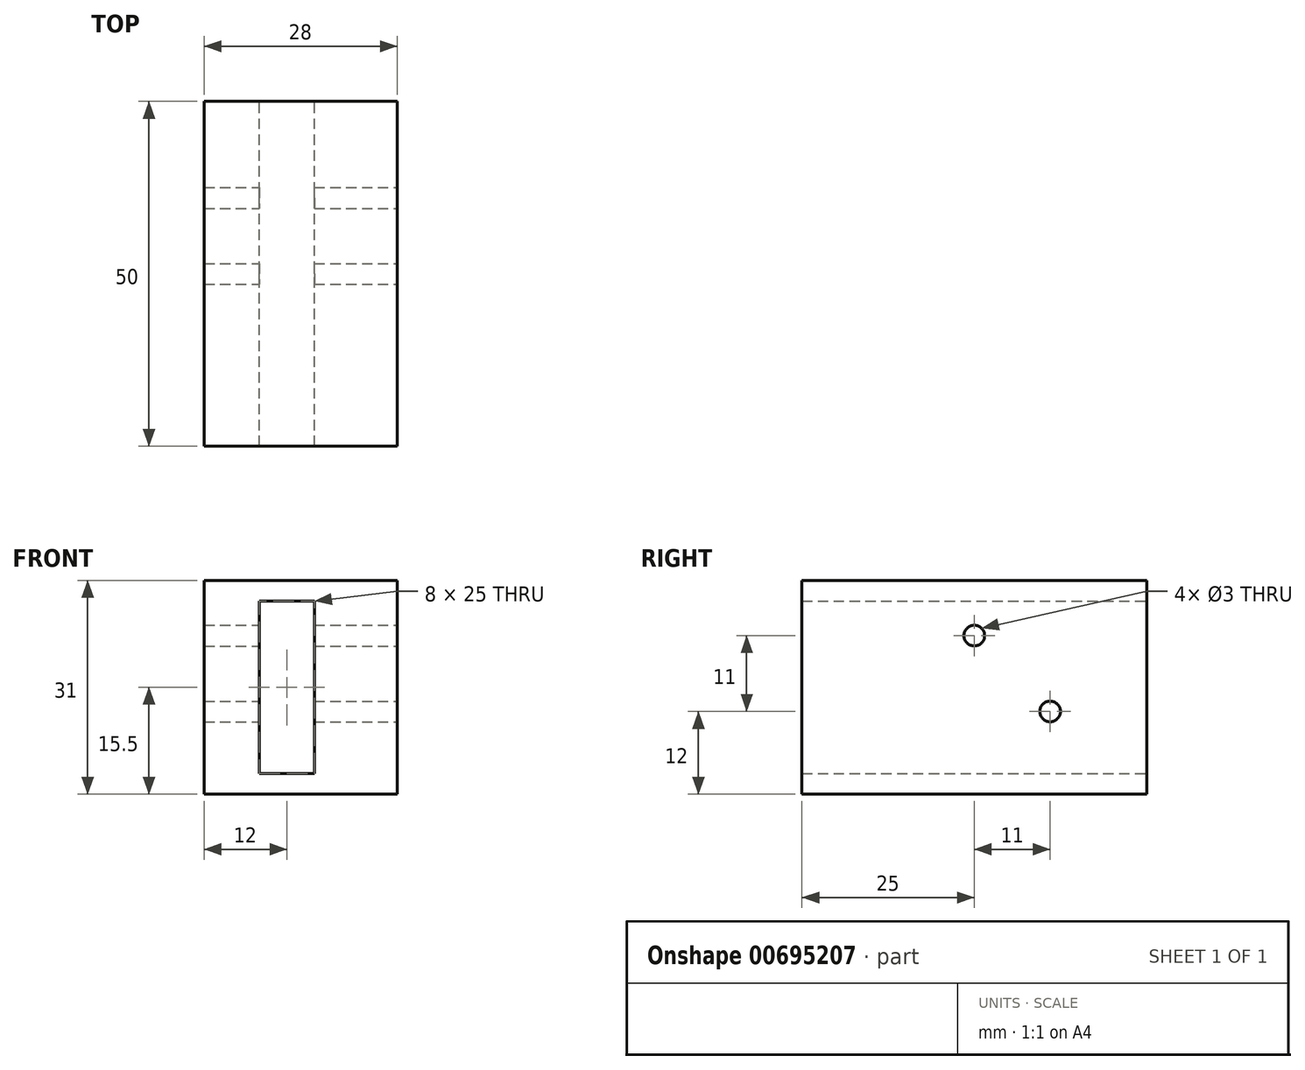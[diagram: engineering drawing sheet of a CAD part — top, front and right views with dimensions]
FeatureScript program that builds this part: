
annotation { "Feature Type Name" : "Feature", "Feature Type Description" : "" }
export const myFeature = defineFeature(function(context is Context, id is Id, definition is map)
    precondition{}
    {
        {
            var Q0;
            Q0=qCreatedBy(makeId("Top.planeOp"),FACE);
            var sketch = newSketch(context, id + "F0", { "sketchPlane" : qUnion([Q0])});
            skLineSegment(sketch, "E0.bottom", {"start": v(0, 0) * mm, "end": v(28, 0) * mm});
            skLineSegment(sketch, "E0.top", {"start": v(0, 50) * mm, "end": v(28, 50) * mm});
            skLineSegment(sketch, "E0.left", {"start": v(0, 0) * mm, "end": v(0, 50) * mm});
            skLineSegment(sketch, "E0.right", {"start": v(28, 0) * mm, "end": v(28, 50) * mm});
            skSolve(sketch);
        }
        {
            var Q0;
            Q0=makeQuery(id+"F0.imprint","IMPRINT",FACE,{"disambiguationData":[TD([[makeQuery(id+"F0.imprint","IMPRINT",EDGE,{"derivedFrom":sQuery(id+"F0.wireOp",EDGE,"E0.bottom")}),1.0]])]});
            extrude(context, id + "F1", {"entities" : qUnion([Q0]), "depth" : 3 * mm, "offsetDistance" : 25 * mm});
        }
        {
            var Q0;
            Q0=makeQuery(id+"F1.opExtrude","CAP_FACE",FACE,{"disambiguationData":[OSD([sQuery(id+"F0.wireOp",EDGE,"E0.bottom"),sQuery(id+"F0.wireOp",EDGE,"E0.top"),sQuery(id+"F0.wireOp",EDGE,"E0.left"),sQuery(id+"F0.wireOp",EDGE,"E0.right")])],"isStart":false});
            var sketch = newSketch(context, id + "F2", { "sketchPlane" : qUnion([Q0])});
            skLineSegment(sketch, "E1.bottom", {"start": v(28, 0) * mm, "end": v(16, 0) * mm});
            skLineSegment(sketch, "E1.top", {"start": v(28, 50) * mm, "end": v(16, 50) * mm});
            skLineSegment(sketch, "E1.left", {"start": v(28, 0) * mm, "end": v(28, 50) * mm});
            skLineSegment(sketch, "E1.right", {"start": v(16, 0) * mm, "end": v(16, 50) * mm});
            skLineSegment(sketch, "E2.bottom", {"start": v(16, 0) * mm, "end": v(8, 0) * mm});
            skLineSegment(sketch, "E2.top", {"start": v(16, 50) * mm, "end": v(8, 50) * mm});
            skLineSegment(sketch, "E2.right", {"start": v(8, 0) * mm, "end": v(8, 50) * mm});
            skLineSegment(sketch, "E3.bottom", {"start": v(8, 50) * mm, "end": v(0, 50) * mm});
            skLineSegment(sketch, "E3.top", {"start": v(8, 0) * mm, "end": v(0, 0) * mm});
            skLineSegment(sketch, "E3.left", {"start": v(8, 50) * mm, "end": v(8, 0) * mm});
            skLineSegment(sketch, "E3.right", {"start": v(0, 50) * mm, "end": v(0, 0) * mm});
            skSolve(sketch);
        }
        {
            var Q0;
            Q0=makeQuery(id+"F2.imprint","IMPRINT",FACE,{"disambiguationData":[TD([[makeQuery(id+"F2.imprint","IMPRINT",EDGE,{"derivedFrom":sQuery(id+"F2.wireOp",EDGE,"E3.bottom")}),-1.0]])]});
            var Q1;
            Q1=makeQuery(id+"F2.imprint","IMPRINT",FACE,{"disambiguationData":[TD([[makeQuery(id+"F2.imprint","IMPRINT",EDGE,{"derivedFrom":sQuery(id+"F2.wireOp",EDGE,"E1.bottom")}),1.0]])]});
            extrude(context, id + "F3", {"entities" : qUnion([Q0, Q1]), "operationType" : NewBodyOperationType.ADD, "depth" : 25 * mm, "offsetDistance" : 25 * mm});
        }
        {
            var Q0;
            Q0=makeQuery(id+"F3.opExtrude","CAP_FACE",FACE,{"disambiguationData":[OSD([sQuery(id+"F2.wireOp",EDGE,"E3.bottom"),sQuery(id+"F2.wireOp",EDGE,"E3.top"),sQuery(id+"F2.wireOp",EDGE,"E3.left"),sQuery(id+"F2.wireOp",EDGE,"E3.right")])],"isStart":false});
            var sketch = newSketch(context, id + "F4", { "sketchPlane" : qUnion([Q0])});
            skLineSegment(sketch, "E4", {"start": v(0, 0) * mm, "end": v(0, 50) * mm});
            skLineSegment(sketch, "E5", {"start": v(0, 50) * mm, "end": v(28, 50) * mm});
            skLineSegment(sketch, "E6", {"start": v(28, 50) * mm, "end": v(28, 0) * mm});
            skLineSegment(sketch, "E7", {"start": v(28, 0) * mm, "end": v(0, 0) * mm});
            skSolve(sketch);
        }
        {
            var Q0;
            {var subQ2=sQuery(id+"F4.wireOp",EDGE,"E6");Q0=makeQuery(id+"F4.imprint","IMPRINT",FACE,{"disambiguationData":[TD([[makeQuery(id+"F4.imprint","IMPRINT",EDGE,{"derivedFrom":subQ2}),-1.0]])]});}
            var Q1;
            {var subQ0=sQuery(id+"F4.wireOp",EDGE,"E4");Q1=makeQuery(id+"F4.imprint","IMPRINT",FACE,{"disambiguationData":[TD([[makeQuery(id+"F4.imprint","IMPRINT",EDGE,{"derivedFrom":subQ0}),-1.0]])]});}
            extrude(context, id + "F5", {"entities" : qUnion([Q0, Q1]), "operationType" : NewBodyOperationType.ADD, "depth" : 3 * mm, "offsetDistance" : 25 * mm});
        }
        {
            var Q0;
            Q0=makeQuery(id+"F5.boolean.opBoolean","MERGE",FACE,{"derivedFrom":[makeQuery(id+"F3.boolean.opBoolean","MERGE",FACE,{"derivedFrom":[makeQuery(id+"F1.opExtrude","SWEPT_FACE",FACE,{"disambiguationData":[OSD([sQuery(id+"F0.wireOp",EDGE,"E0.right")])]}),makeQuery(id+"F3.opExtrude","SWEPT_FACE",FACE,{"disambiguationData":[OSD([sQuery(id+"F2.wireOp",EDGE,"E1.left")])]})]}),makeQuery(id+"F5.opExtrude","SWEPT_FACE",FACE,{"disambiguationData":[OSD([sQuery(id+"F4.wireOp",EDGE,"E6")])]})]});
            var sketch = newSketch(context, id + "F6", { "sketchPlane" : qUnion([Q0])});
            skLineSegment(sketch, "E8", {"start": v(36, 31) * mm, "end": v(36, 12) * mm});
            skLineSegment(sketch, "E9", {"start": v(36, 31) * mm, "end": v(50, 31) * mm});
            skLineSegment(sketch, "E10", {"start": v(36, 31) * mm, "end": v(25, 31) * mm});
            skLineSegment(sketch, "E11", {"start": v(25, 31) * mm, "end": v(25, 23) * mm});
            skCircle(sketch, "E12", {"center": v(25, 23) * mm, "radius": 1.5 * mm});
            skCircle(sketch, "E13", {"center": v(36, 12) * mm, "radius": 1.5 * mm});
            skSolve(sketch);
        }
        {
            var Q0;
            Q0=makeQuery(id+"F6.imprint","IMPRINT",FACE,{"disambiguationData":[TD([[makeQuery(id+"F6.imprint","IMPRINT",EDGE,{"derivedFrom":sQuery(id+"F6.wireOp",EDGE,"E12")}),1.0]])]});
            var Q1;
            Q1=makeQuery(id+"F6.imprint","IMPRINT",FACE,{"disambiguationData":[TD([[makeQuery(id+"F6.imprint","IMPRINT",EDGE,{"derivedFrom":sQuery(id+"F6.wireOp",EDGE,"E13")}),1.0]])]});
            extrude(context, id + "F7", {"entities" : qUnion([Q0, Q1]), "operationType" : NewBodyOperationType.REMOVE, "oppositeDirection" : true, "depth" : 67.4 * mm, "offsetDistance" : 25 * mm});
        }
    });
